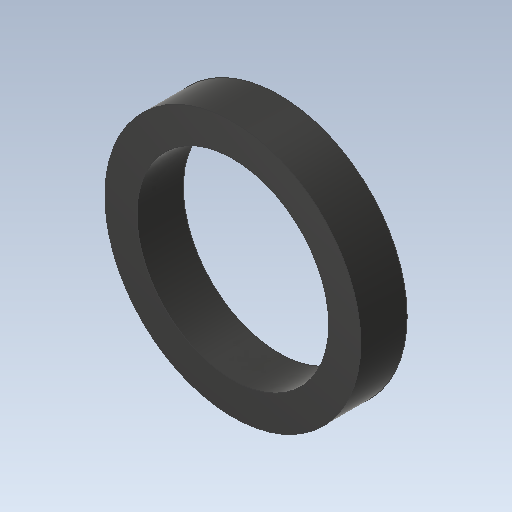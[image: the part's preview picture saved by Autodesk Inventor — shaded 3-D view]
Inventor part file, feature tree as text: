
AUTODESK INVENTOR PART (.ipt)
format: ipt  version: 2020.2 (Build 242310000, 310)  size: 97,280 bytes
history: native  units: mm
features: other x1, extrude x1, sketch x1
ambient origin geometry x8: Origin, YZ Plane, XZ Plane, XY Plane, X Axis, Y Axis, Z Axis, Center Point
bodies: Body1 (feature_tree)
feature tree (3):
  other  "ソリッド1"
  extrude  "押し出し1"  Depth=6.0mm
  sketch  "スケッチ1"
